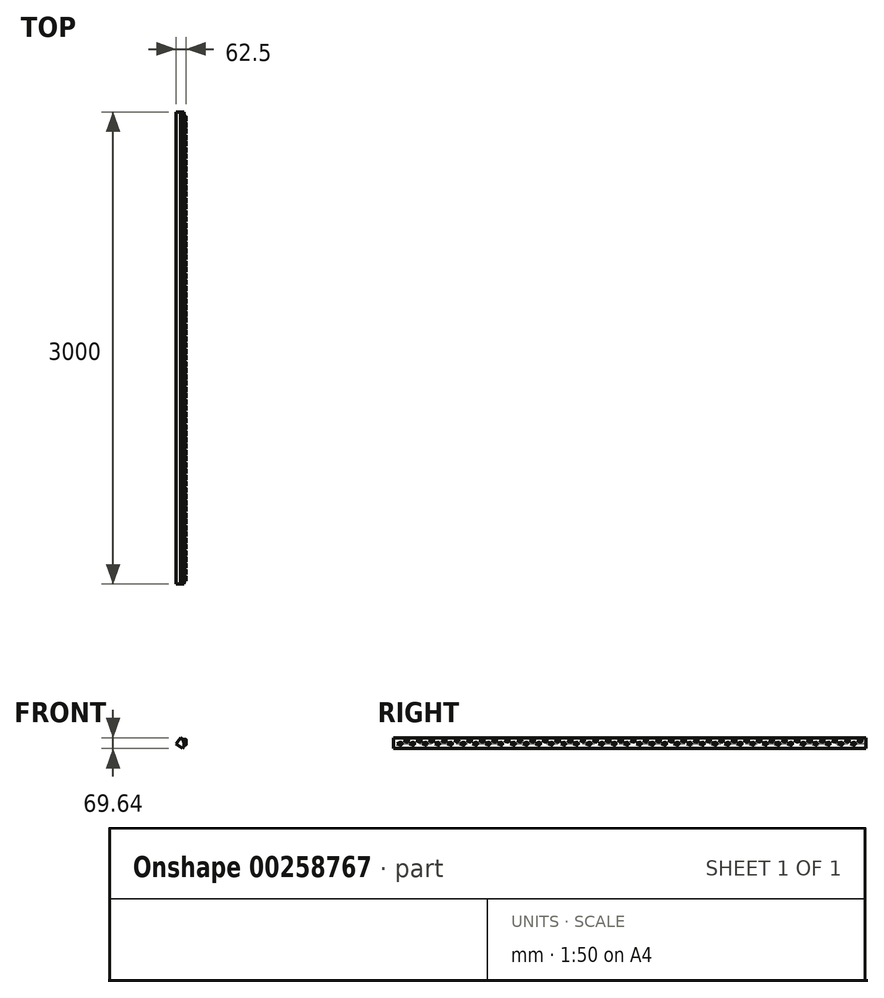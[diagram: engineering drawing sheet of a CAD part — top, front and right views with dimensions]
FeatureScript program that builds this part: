
annotation { "Feature Type Name" : "Feature", "Feature Type Description" : "" }
export const myFeature = defineFeature(function(context is Context, id is Id, definition is map)
    precondition{}
    {
        {
            var Q0;
            Q0=qCreatedBy(makeId("Front.planeOp"),FACE);
            var sketch = newSketch(context, id + "F0", { "sketchPlane" : qUnion([Q0])});
            skArc(sketch, "E0", {"start": v(40.96, -28.68) * mm, "mid": v(49.24, 8.68) * mm, "end": v(28.68, 40.96) * mm});
            skLineSegment(sketch, "E1", {"start": v(0, 0) * mm, "end": v(28.68, 40.96) * mm});
            skLineSegment(sketch, "E2", {"start": v(0, 0) * mm, "end": v(40.96, -28.68) * mm});
            skSolve(sketch);
        }
        {
            var Q0;
            Q0 = qSketchRegion(id + "F0", true);
            extrude(context, id + "F1", {"entities" : qUnion([Q0]), "oppositeDirection" : true, "depth" : 3000 * mm});
        }
        {
            var Q0;
            Q0=qCreatedBy(makeId("Right.planeOp"),FACE);
            cPlane(context, id + "F2", {"entities" : qUnion([Q0]), "cplaneType" : CPlaneType.OFFSET, "offset" : 50 * mm, "width" : 150 * mm, "height" : 150 * mm});
        }
        {
            var Q0;
            Q0=qCreatedBy(id+"F2.planeOp",FACE);
            var sketch = newSketch(context, id + "F3", { "sketchPlane" : qUnion([Q0])});
            skLineSegment(sketch, "E3", {"start": v(21.54, 0) * mm, "end": v(38.71, 10.26) * mm});
            skLineSegment(sketch, "E4", {"start": v(21.54, 0) * mm, "end": v(40.62, -6) * mm});
            skArc(sketch, "E5", {"start": v(40.62, -6) * mm, "mid": v(52.32, 3.61) * mm, "end": v(38.71, 10.26) * mm});
            skLineSegment(sketch, "E6.1.0.0", {"start": v(101.54, 0) * mm, "end": v(118.71, 10.26) * mm});
            skLineSegment(sketch, "E6.1.0.1", {"start": v(101.54, 0) * mm, "end": v(120.62, -6) * mm});
            skArc(sketch, "E6.1.0.2", {"start": v(120.62, -6) * mm, "mid": v(132.32, 3.61) * mm, "end": v(118.71, 10.26) * mm});
            skLineSegment(sketch, "E6.2.0.0", {"start": v(181.54, 0) * mm, "end": v(198.71, 10.26) * mm});
            skLineSegment(sketch, "E6.2.0.1", {"start": v(181.54, 0) * mm, "end": v(200.62, -6) * mm});
            skArc(sketch, "E6.2.0.2", {"start": v(200.62, -6) * mm, "mid": v(212.32, 3.61) * mm, "end": v(198.71, 10.26) * mm});
            skLineSegment(sketch, "E6.3.0.0", {"start": v(261.54, 0) * mm, "end": v(278.71, 10.26) * mm});
            skLineSegment(sketch, "E6.3.0.1", {"start": v(261.54, 0) * mm, "end": v(280.62, -6) * mm});
            skArc(sketch, "E6.3.0.2", {"start": v(280.62, -6) * mm, "mid": v(292.32, 3.61) * mm, "end": v(278.71, 10.26) * mm});
            skLineSegment(sketch, "E6.4.0.0", {"start": v(341.54, 0) * mm, "end": v(358.71, 10.26) * mm});
            skLineSegment(sketch, "E6.4.0.1", {"start": v(341.54, 0) * mm, "end": v(360.62, -6) * mm});
            skArc(sketch, "E6.4.0.2", {"start": v(360.62, -6) * mm, "mid": v(372.32, 3.61) * mm, "end": v(358.71, 10.26) * mm});
            skLineSegment(sketch, "E6.5.0.0", {"start": v(421.54, 0) * mm, "end": v(438.71, 10.26) * mm});
            skLineSegment(sketch, "E6.5.0.1", {"start": v(421.54, 0) * mm, "end": v(440.62, -6) * mm});
            skArc(sketch, "E6.5.0.2", {"start": v(440.62, -6) * mm, "mid": v(452.32, 3.61) * mm, "end": v(438.71, 10.26) * mm});
            skLineSegment(sketch, "E6.6.0.0", {"start": v(501.54, 0) * mm, "end": v(518.71, 10.26) * mm});
            skLineSegment(sketch, "E6.6.0.1", {"start": v(501.54, 0) * mm, "end": v(520.62, -6) * mm});
            skArc(sketch, "E6.6.0.2", {"start": v(520.62, -6) * mm, "mid": v(532.32, 3.61) * mm, "end": v(518.71, 10.26) * mm});
            skLineSegment(sketch, "E6.7.0.0", {"start": v(581.54, 0) * mm, "end": v(598.71, 10.26) * mm});
            skLineSegment(sketch, "E6.7.0.1", {"start": v(581.54, 0) * mm, "end": v(600.62, -6) * mm});
            skArc(sketch, "E6.7.0.2", {"start": v(600.62, -6) * mm, "mid": v(612.32, 3.61) * mm, "end": v(598.71, 10.26) * mm});
            skLineSegment(sketch, "E6.8.0.0", {"start": v(661.54, 0) * mm, "end": v(678.71, 10.26) * mm});
            skLineSegment(sketch, "E6.8.0.1", {"start": v(661.54, 0) * mm, "end": v(680.62, -6) * mm});
            skArc(sketch, "E6.8.0.2", {"start": v(680.62, -6) * mm, "mid": v(692.32, 3.61) * mm, "end": v(678.71, 10.26) * mm});
            skLineSegment(sketch, "E6.9.0.0", {"start": v(741.54, 0) * mm, "end": v(758.71, 10.26) * mm});
            skLineSegment(sketch, "E6.9.0.1", {"start": v(741.54, 0) * mm, "end": v(760.62, -6) * mm});
            skArc(sketch, "E6.9.0.2", {"start": v(760.62, -6) * mm, "mid": v(772.32, 3.61) * mm, "end": v(758.71, 10.26) * mm});
            skLineSegment(sketch, "E6.10.0.0", {"start": v(821.54, 0) * mm, "end": v(838.71, 10.26) * mm});
            skLineSegment(sketch, "E6.10.0.1", {"start": v(821.54, 0) * mm, "end": v(840.62, -6) * mm});
            skArc(sketch, "E6.10.0.2", {"start": v(840.62, -6) * mm, "mid": v(852.32, 3.61) * mm, "end": v(838.71, 10.26) * mm});
            skLineSegment(sketch, "E6.11.0.0", {"start": v(901.54, 0) * mm, "end": v(918.71, 10.26) * mm});
            skLineSegment(sketch, "E6.11.0.1", {"start": v(901.54, 0) * mm, "end": v(920.62, -6) * mm});
            skArc(sketch, "E6.11.0.2", {"start": v(920.62, -6) * mm, "mid": v(932.32, 3.61) * mm, "end": v(918.71, 10.26) * mm});
            skLineSegment(sketch, "E6.12.0.0", {"start": v(981.54, 0) * mm, "end": v(998.71, 10.26) * mm});
            skLineSegment(sketch, "E6.12.0.1", {"start": v(981.54, 0) * mm, "end": v(1000.62, -6) * mm});
            skArc(sketch, "E6.12.0.2", {"start": v(1000.62, -6) * mm, "mid": v(1012.32, 3.61) * mm, "end": v(998.71, 10.26) * mm});
            skLineSegment(sketch, "E6.13.0.0", {"start": v(1061.54, 0) * mm, "end": v(1078.71, 10.26) * mm});
            skLineSegment(sketch, "E6.13.0.1", {"start": v(1061.54, 0) * mm, "end": v(1080.62, -6) * mm});
            skArc(sketch, "E6.13.0.2", {"start": v(1080.62, -6) * mm, "mid": v(1092.32, 3.61) * mm, "end": v(1078.71, 10.26) * mm});
            skLineSegment(sketch, "E6.14.0.0", {"start": v(1141.54, 0) * mm, "end": v(1158.71, 10.26) * mm});
            skLineSegment(sketch, "E6.14.0.1", {"start": v(1141.54, 0) * mm, "end": v(1160.62, -6) * mm});
            skArc(sketch, "E6.14.0.2", {"start": v(1160.62, -6) * mm, "mid": v(1172.32, 3.61) * mm, "end": v(1158.71, 10.26) * mm});
            skLineSegment(sketch, "E6.15.0.0", {"start": v(1221.54, 0) * mm, "end": v(1238.71, 10.26) * mm});
            skLineSegment(sketch, "E6.15.0.1", {"start": v(1221.54, 0) * mm, "end": v(1240.62, -6) * mm});
            skArc(sketch, "E6.15.0.2", {"start": v(1240.62, -6) * mm, "mid": v(1252.32, 3.61) * mm, "end": v(1238.71, 10.26) * mm});
            skLineSegment(sketch, "E6.16.0.0", {"start": v(1301.54, 0) * mm, "end": v(1318.71, 10.26) * mm});
            skLineSegment(sketch, "E6.16.0.1", {"start": v(1301.54, 0) * mm, "end": v(1320.62, -6) * mm});
            skArc(sketch, "E6.16.0.2", {"start": v(1320.62, -6) * mm, "mid": v(1332.32, 3.61) * mm, "end": v(1318.71, 10.26) * mm});
            skLineSegment(sketch, "E6.17.0.0", {"start": v(1381.54, 0) * mm, "end": v(1398.71, 10.26) * mm});
            skLineSegment(sketch, "E6.17.0.1", {"start": v(1381.54, 0) * mm, "end": v(1400.62, -6) * mm});
            skArc(sketch, "E6.17.0.2", {"start": v(1400.62, -6) * mm, "mid": v(1412.32, 3.61) * mm, "end": v(1398.71, 10.26) * mm});
            skLineSegment(sketch, "E6.18.0.0", {"start": v(1461.54, 0) * mm, "end": v(1478.71, 10.26) * mm});
            skLineSegment(sketch, "E6.18.0.1", {"start": v(1461.54, 0) * mm, "end": v(1480.62, -6) * mm});
            skArc(sketch, "E6.18.0.2", {"start": v(1480.62, -6) * mm, "mid": v(1492.32, 3.61) * mm, "end": v(1478.71, 10.26) * mm});
            skLineSegment(sketch, "E6.19.0.0", {"start": v(1541.54, 0) * mm, "end": v(1558.71, 10.26) * mm});
            skLineSegment(sketch, "E6.19.0.1", {"start": v(1541.54, 0) * mm, "end": v(1560.62, -6) * mm});
            skArc(sketch, "E6.19.0.2", {"start": v(1560.62, -6) * mm, "mid": v(1572.32, 3.61) * mm, "end": v(1558.71, 10.26) * mm});
            skLineSegment(sketch, "E6.20.0.0", {"start": v(1621.54, 0) * mm, "end": v(1638.71, 10.26) * mm});
            skLineSegment(sketch, "E6.20.0.1", {"start": v(1621.54, 0) * mm, "end": v(1640.62, -6) * mm});
            skArc(sketch, "E6.20.0.2", {"start": v(1640.62, -6) * mm, "mid": v(1652.32, 3.61) * mm, "end": v(1638.71, 10.26) * mm});
            skLineSegment(sketch, "E6.21.0.0", {"start": v(1701.54, 0) * mm, "end": v(1718.71, 10.26) * mm});
            skLineSegment(sketch, "E6.21.0.1", {"start": v(1701.54, 0) * mm, "end": v(1720.62, -6) * mm});
            skArc(sketch, "E6.21.0.2", {"start": v(1720.62, -6) * mm, "mid": v(1732.32, 3.61) * mm, "end": v(1718.71, 10.26) * mm});
            skLineSegment(sketch, "E6.22.0.0", {"start": v(1781.54, 0) * mm, "end": v(1798.71, 10.26) * mm});
            skLineSegment(sketch, "E6.22.0.1", {"start": v(1781.54, 0) * mm, "end": v(1800.62, -6) * mm});
            skArc(sketch, "E6.22.0.2", {"start": v(1800.62, -6) * mm, "mid": v(1812.32, 3.61) * mm, "end": v(1798.71, 10.26) * mm});
            skLineSegment(sketch, "E6.23.0.0", {"start": v(1861.54, 0) * mm, "end": v(1878.71, 10.26) * mm});
            skLineSegment(sketch, "E6.23.0.1", {"start": v(1861.54, 0) * mm, "end": v(1880.62, -6) * mm});
            skArc(sketch, "E6.23.0.2", {"start": v(1880.62, -6) * mm, "mid": v(1892.32, 3.61) * mm, "end": v(1878.71, 10.26) * mm});
            skLineSegment(sketch, "E6.24.0.0", {"start": v(1941.54, 0) * mm, "end": v(1958.71, 10.26) * mm});
            skLineSegment(sketch, "E6.24.0.1", {"start": v(1941.54, 0) * mm, "end": v(1960.62, -6) * mm});
            skArc(sketch, "E6.24.0.2", {"start": v(1960.62, -6) * mm, "mid": v(1972.32, 3.61) * mm, "end": v(1958.71, 10.26) * mm});
            skLineSegment(sketch, "E6.25.0.0", {"start": v(2021.54, 0) * mm, "end": v(2038.71, 10.26) * mm});
            skLineSegment(sketch, "E6.25.0.1", {"start": v(2021.54, 0) * mm, "end": v(2040.62, -6) * mm});
            skArc(sketch, "E6.25.0.2", {"start": v(2040.62, -6) * mm, "mid": v(2052.32, 3.61) * mm, "end": v(2038.71, 10.26) * mm});
            skLineSegment(sketch, "E6.26.0.0", {"start": v(2101.54, 0) * mm, "end": v(2118.71, 10.26) * mm});
            skLineSegment(sketch, "E6.26.0.1", {"start": v(2101.54, 0) * mm, "end": v(2120.62, -6) * mm});
            skArc(sketch, "E6.26.0.2", {"start": v(2120.62, -6) * mm, "mid": v(2132.32, 3.61) * mm, "end": v(2118.71, 10.26) * mm});
            skLineSegment(sketch, "E6.27.0.0", {"start": v(2181.54, 0) * mm, "end": v(2198.71, 10.26) * mm});
            skLineSegment(sketch, "E6.27.0.1", {"start": v(2181.54, 0) * mm, "end": v(2200.62, -6) * mm});
            skArc(sketch, "E6.27.0.2", {"start": v(2200.62, -6) * mm, "mid": v(2212.32, 3.61) * mm, "end": v(2198.71, 10.26) * mm});
            skLineSegment(sketch, "E6.28.0.0", {"start": v(2261.54, 0) * mm, "end": v(2278.71, 10.26) * mm});
            skLineSegment(sketch, "E6.28.0.1", {"start": v(2261.54, 0) * mm, "end": v(2280.62, -6) * mm});
            skArc(sketch, "E6.28.0.2", {"start": v(2280.62, -6) * mm, "mid": v(2292.32, 3.61) * mm, "end": v(2278.71, 10.26) * mm});
            skLineSegment(sketch, "E6.29.0.0", {"start": v(2341.54, 0) * mm, "end": v(2358.71, 10.26) * mm});
            skLineSegment(sketch, "E6.29.0.1", {"start": v(2341.54, 0) * mm, "end": v(2360.62, -6) * mm});
            skArc(sketch, "E6.29.0.2", {"start": v(2360.62, -6) * mm, "mid": v(2372.32, 3.61) * mm, "end": v(2358.71, 10.26) * mm});
            skLineSegment(sketch, "E6.direction1", {"start": v(21.54, 0) * mm, "end": v(101.54, 0) * mm, "construction": true});
            skLineSegment(sketch, "E7.0.30.0", {"start": v(2421.54, 0) * mm, "end": v(2438.71, 10.26) * mm});
            skLineSegment(sketch, "E7.3.30.0", {"start": v(2421.54, 0) * mm, "end": v(2440.62, -6) * mm});
            skArc(sketch, "E7.6.30.0", {"start": v(2440.62, -6) * mm, "mid": v(2452.32, 3.61) * mm, "end": v(2438.71, 10.26) * mm});
            skLineSegment(sketch, "E7.0.31.0", {"start": v(2501.54, 0) * mm, "end": v(2518.71, 10.26) * mm});
            skLineSegment(sketch, "E7.3.31.0", {"start": v(2501.54, 0) * mm, "end": v(2520.62, -6) * mm});
            skArc(sketch, "E7.6.31.0", {"start": v(2520.62, -6) * mm, "mid": v(2532.32, 3.61) * mm, "end": v(2518.71, 10.26) * mm});
            skLineSegment(sketch, "E7.0.32.0", {"start": v(2581.54, 0) * mm, "end": v(2598.71, 10.26) * mm});
            skLineSegment(sketch, "E7.3.32.0", {"start": v(2581.54, 0) * mm, "end": v(2600.62, -6) * mm});
            skArc(sketch, "E7.6.32.0", {"start": v(2600.62, -6) * mm, "mid": v(2612.32, 3.61) * mm, "end": v(2598.71, 10.26) * mm});
            skLineSegment(sketch, "E7.0.33.0", {"start": v(2661.54, 0) * mm, "end": v(2678.71, 10.26) * mm});
            skLineSegment(sketch, "E7.3.33.0", {"start": v(2661.54, 0) * mm, "end": v(2680.62, -6) * mm});
            skArc(sketch, "E7.6.33.0", {"start": v(2680.62, -6) * mm, "mid": v(2692.32, 3.61) * mm, "end": v(2678.71, 10.26) * mm});
            skLineSegment(sketch, "E7.0.34.0", {"start": v(2741.54, 0) * mm, "end": v(2758.71, 10.26) * mm});
            skLineSegment(sketch, "E7.3.34.0", {"start": v(2741.54, 0) * mm, "end": v(2760.62, -6) * mm});
            skArc(sketch, "E7.6.34.0", {"start": v(2760.62, -6) * mm, "mid": v(2772.32, 3.61) * mm, "end": v(2758.71, 10.26) * mm});
            skLineSegment(sketch, "E8.0.35.0", {"start": v(2821.54, 0) * mm, "end": v(2838.71, 10.26) * mm});
            skLineSegment(sketch, "E8.3.35.0", {"start": v(2821.54, 0) * mm, "end": v(2840.62, -6) * mm});
            skArc(sketch, "E8.6.35.0", {"start": v(2840.62, -6) * mm, "mid": v(2852.32, 3.61) * mm, "end": v(2838.71, 10.26) * mm});
            skLineSegment(sketch, "E8.0.36.0", {"start": v(2901.54, 0) * mm, "end": v(2918.71, 10.26) * mm});
            skLineSegment(sketch, "E8.3.36.0", {"start": v(2901.54, 0) * mm, "end": v(2920.62, -6) * mm});
            skArc(sketch, "E8.6.36.0", {"start": v(2920.62, -6) * mm, "mid": v(2932.32, 3.61) * mm, "end": v(2918.71, 10.26) * mm});
            skLineSegment(sketch, "E9", {"start": v(62.38, 22.39) * mm, "end": v(80.62, 30.6) * mm});
            skLineSegment(sketch, "E10", {"start": v(62.38, 22.39) * mm, "end": v(80.62, 14.18) * mm});
            skArc(sketch, "E11", {"start": v(80.62, 14.18) * mm, "mid": v(93.31, 22.39) * mm, "end": v(80.62, 30.6) * mm});
            skLineSegment(sketch, "E12.1.0.0", {"start": v(142.38, 22.39) * mm, "end": v(160.62, 30.6) * mm});
            skLineSegment(sketch, "E12.1.0.1", {"start": v(142.38, 22.39) * mm, "end": v(160.62, 14.18) * mm});
            skArc(sketch, "E12.1.0.2", {"start": v(160.62, 14.18) * mm, "mid": v(173.31, 22.39) * mm, "end": v(160.62, 30.6) * mm});
            skLineSegment(sketch, "E12.2.0.0", {"start": v(222.38, 22.39) * mm, "end": v(240.62, 30.6) * mm});
            skLineSegment(sketch, "E12.2.0.1", {"start": v(222.38, 22.39) * mm, "end": v(240.62, 14.18) * mm});
            skArc(sketch, "E12.2.0.2", {"start": v(240.62, 14.18) * mm, "mid": v(253.31, 22.39) * mm, "end": v(240.62, 30.6) * mm});
            skLineSegment(sketch, "E12.3.0.0", {"start": v(302.38, 22.39) * mm, "end": v(320.62, 30.6) * mm});
            skLineSegment(sketch, "E12.3.0.1", {"start": v(302.38, 22.39) * mm, "end": v(320.62, 14.18) * mm});
            skArc(sketch, "E12.3.0.2", {"start": v(320.62, 14.18) * mm, "mid": v(333.31, 22.39) * mm, "end": v(320.62, 30.6) * mm});
            skLineSegment(sketch, "E12.4.0.0", {"start": v(382.38, 22.39) * mm, "end": v(400.62, 30.6) * mm});
            skLineSegment(sketch, "E12.4.0.1", {"start": v(382.38, 22.39) * mm, "end": v(400.62, 14.18) * mm});
            skArc(sketch, "E12.4.0.2", {"start": v(400.62, 14.18) * mm, "mid": v(413.31, 22.39) * mm, "end": v(400.62, 30.6) * mm});
            skLineSegment(sketch, "E12.5.0.0", {"start": v(462.38, 22.39) * mm, "end": v(480.62, 30.6) * mm});
            skLineSegment(sketch, "E12.5.0.1", {"start": v(462.38, 22.39) * mm, "end": v(480.62, 14.18) * mm});
            skArc(sketch, "E12.5.0.2", {"start": v(480.62, 14.18) * mm, "mid": v(493.31, 22.39) * mm, "end": v(480.62, 30.6) * mm});
            skLineSegment(sketch, "E12.6.0.0", {"start": v(542.38, 22.39) * mm, "end": v(560.62, 30.6) * mm});
            skLineSegment(sketch, "E12.6.0.1", {"start": v(542.38, 22.39) * mm, "end": v(560.62, 14.18) * mm});
            skArc(sketch, "E12.6.0.2", {"start": v(560.62, 14.18) * mm, "mid": v(573.31, 22.39) * mm, "end": v(560.62, 30.6) * mm});
            skLineSegment(sketch, "E12.7.0.0", {"start": v(622.38, 22.39) * mm, "end": v(640.62, 30.6) * mm});
            skLineSegment(sketch, "E12.7.0.1", {"start": v(622.38, 22.39) * mm, "end": v(640.62, 14.18) * mm});
            skArc(sketch, "E12.7.0.2", {"start": v(640.62, 14.18) * mm, "mid": v(653.31, 22.39) * mm, "end": v(640.62, 30.6) * mm});
            skLineSegment(sketch, "E12.8.0.0", {"start": v(702.38, 22.39) * mm, "end": v(720.62, 30.6) * mm});
            skLineSegment(sketch, "E12.8.0.1", {"start": v(702.38, 22.39) * mm, "end": v(720.62, 14.18) * mm});
            skArc(sketch, "E12.8.0.2", {"start": v(720.62, 14.18) * mm, "mid": v(733.31, 22.39) * mm, "end": v(720.62, 30.6) * mm});
            skLineSegment(sketch, "E12.9.0.0", {"start": v(782.38, 22.39) * mm, "end": v(800.62, 30.6) * mm});
            skLineSegment(sketch, "E12.9.0.1", {"start": v(782.38, 22.39) * mm, "end": v(800.62, 14.18) * mm});
            skArc(sketch, "E12.9.0.2", {"start": v(800.62, 14.18) * mm, "mid": v(813.31, 22.39) * mm, "end": v(800.62, 30.6) * mm});
            skLineSegment(sketch, "E12.10.0.0", {"start": v(862.38, 22.39) * mm, "end": v(880.62, 30.6) * mm});
            skLineSegment(sketch, "E12.10.0.1", {"start": v(862.38, 22.39) * mm, "end": v(880.62, 14.18) * mm});
            skArc(sketch, "E12.10.0.2", {"start": v(880.62, 14.18) * mm, "mid": v(893.31, 22.39) * mm, "end": v(880.62, 30.6) * mm});
            skLineSegment(sketch, "E12.11.0.0", {"start": v(942.38, 22.39) * mm, "end": v(960.62, 30.6) * mm});
            skLineSegment(sketch, "E12.11.0.1", {"start": v(942.38, 22.39) * mm, "end": v(960.62, 14.18) * mm});
            skArc(sketch, "E12.11.0.2", {"start": v(960.62, 14.18) * mm, "mid": v(973.31, 22.39) * mm, "end": v(960.62, 30.6) * mm});
            skLineSegment(sketch, "E12.12.0.0", {"start": v(1022.38, 22.39) * mm, "end": v(1040.62, 30.6) * mm});
            skLineSegment(sketch, "E12.12.0.1", {"start": v(1022.38, 22.39) * mm, "end": v(1040.62, 14.18) * mm});
            skArc(sketch, "E12.12.0.2", {"start": v(1040.62, 14.18) * mm, "mid": v(1053.31, 22.39) * mm, "end": v(1040.62, 30.6) * mm});
            skLineSegment(sketch, "E12.13.0.0", {"start": v(1102.38, 22.39) * mm, "end": v(1120.62, 30.6) * mm});
            skLineSegment(sketch, "E12.13.0.1", {"start": v(1102.38, 22.39) * mm, "end": v(1120.62, 14.18) * mm});
            skArc(sketch, "E12.13.0.2", {"start": v(1120.62, 14.18) * mm, "mid": v(1133.31, 22.39) * mm, "end": v(1120.62, 30.6) * mm});
            skLineSegment(sketch, "E12.14.0.0", {"start": v(1182.38, 22.39) * mm, "end": v(1200.62, 30.6) * mm});
            skLineSegment(sketch, "E12.14.0.1", {"start": v(1182.38, 22.39) * mm, "end": v(1200.62, 14.18) * mm});
            skArc(sketch, "E12.14.0.2", {"start": v(1200.62, 14.18) * mm, "mid": v(1213.31, 22.39) * mm, "end": v(1200.62, 30.6) * mm});
            skLineSegment(sketch, "E12.15.0.0", {"start": v(1262.38, 22.39) * mm, "end": v(1280.62, 30.6) * mm});
            skLineSegment(sketch, "E12.15.0.1", {"start": v(1262.38, 22.39) * mm, "end": v(1280.62, 14.18) * mm});
            skArc(sketch, "E12.15.0.2", {"start": v(1280.62, 14.18) * mm, "mid": v(1293.31, 22.39) * mm, "end": v(1280.62, 30.6) * mm});
            skLineSegment(sketch, "E12.16.0.0", {"start": v(1342.38, 22.39) * mm, "end": v(1360.62, 30.6) * mm});
            skLineSegment(sketch, "E12.16.0.1", {"start": v(1342.38, 22.39) * mm, "end": v(1360.62, 14.18) * mm});
            skArc(sketch, "E12.16.0.2", {"start": v(1360.62, 14.18) * mm, "mid": v(1373.31, 22.39) * mm, "end": v(1360.62, 30.6) * mm});
            skLineSegment(sketch, "E12.17.0.0", {"start": v(1422.38, 22.39) * mm, "end": v(1440.62, 30.6) * mm});
            skLineSegment(sketch, "E12.17.0.1", {"start": v(1422.38, 22.39) * mm, "end": v(1440.62, 14.18) * mm});
            skArc(sketch, "E12.17.0.2", {"start": v(1440.62, 14.18) * mm, "mid": v(1453.31, 22.39) * mm, "end": v(1440.62, 30.6) * mm});
            skLineSegment(sketch, "E12.18.0.0", {"start": v(1502.38, 22.39) * mm, "end": v(1520.62, 30.6) * mm});
            skLineSegment(sketch, "E12.18.0.1", {"start": v(1502.38, 22.39) * mm, "end": v(1520.62, 14.18) * mm});
            skArc(sketch, "E12.18.0.2", {"start": v(1520.62, 14.18) * mm, "mid": v(1533.31, 22.39) * mm, "end": v(1520.62, 30.6) * mm});
            skLineSegment(sketch, "E12.19.0.0", {"start": v(1582.38, 22.39) * mm, "end": v(1600.62, 30.6) * mm});
            skLineSegment(sketch, "E12.19.0.1", {"start": v(1582.38, 22.39) * mm, "end": v(1600.62, 14.18) * mm});
            skArc(sketch, "E12.19.0.2", {"start": v(1600.62, 14.18) * mm, "mid": v(1613.31, 22.39) * mm, "end": v(1600.62, 30.6) * mm});
            skLineSegment(sketch, "E12.20.0.0", {"start": v(1662.38, 22.39) * mm, "end": v(1680.62, 30.6) * mm});
            skLineSegment(sketch, "E12.20.0.1", {"start": v(1662.38, 22.39) * mm, "end": v(1680.62, 14.18) * mm});
            skArc(sketch, "E12.20.0.2", {"start": v(1680.62, 14.18) * mm, "mid": v(1693.31, 22.39) * mm, "end": v(1680.62, 30.6) * mm});
            skLineSegment(sketch, "E12.21.0.0", {"start": v(1742.38, 22.39) * mm, "end": v(1760.62, 30.6) * mm});
            skLineSegment(sketch, "E12.21.0.1", {"start": v(1742.38, 22.39) * mm, "end": v(1760.62, 14.18) * mm});
            skArc(sketch, "E12.21.0.2", {"start": v(1760.62, 14.18) * mm, "mid": v(1773.31, 22.39) * mm, "end": v(1760.62, 30.6) * mm});
            skLineSegment(sketch, "E12.22.0.0", {"start": v(1822.38, 22.39) * mm, "end": v(1840.62, 30.6) * mm});
            skLineSegment(sketch, "E12.22.0.1", {"start": v(1822.38, 22.39) * mm, "end": v(1840.62, 14.18) * mm});
            skArc(sketch, "E12.22.0.2", {"start": v(1840.62, 14.18) * mm, "mid": v(1853.31, 22.39) * mm, "end": v(1840.62, 30.6) * mm});
            skLineSegment(sketch, "E12.23.0.0", {"start": v(1902.38, 22.39) * mm, "end": v(1920.62, 30.6) * mm});
            skLineSegment(sketch, "E12.23.0.1", {"start": v(1902.38, 22.39) * mm, "end": v(1920.62, 14.18) * mm});
            skArc(sketch, "E12.23.0.2", {"start": v(1920.62, 14.18) * mm, "mid": v(1933.31, 22.39) * mm, "end": v(1920.62, 30.6) * mm});
            skLineSegment(sketch, "E12.24.0.0", {"start": v(1982.38, 22.39) * mm, "end": v(2000.62, 30.6) * mm});
            skLineSegment(sketch, "E12.24.0.1", {"start": v(1982.38, 22.39) * mm, "end": v(2000.62, 14.18) * mm});
            skArc(sketch, "E12.24.0.2", {"start": v(2000.62, 14.18) * mm, "mid": v(2013.31, 22.39) * mm, "end": v(2000.62, 30.6) * mm});
            skLineSegment(sketch, "E12.25.0.0", {"start": v(2062.38, 22.39) * mm, "end": v(2080.62, 30.6) * mm});
            skLineSegment(sketch, "E12.25.0.1", {"start": v(2062.38, 22.39) * mm, "end": v(2080.62, 14.18) * mm});
            skArc(sketch, "E12.25.0.2", {"start": v(2080.62, 14.18) * mm, "mid": v(2093.31, 22.39) * mm, "end": v(2080.62, 30.6) * mm});
            skLineSegment(sketch, "E12.26.0.0", {"start": v(2142.38, 22.39) * mm, "end": v(2160.62, 30.6) * mm});
            skLineSegment(sketch, "E12.26.0.1", {"start": v(2142.38, 22.39) * mm, "end": v(2160.62, 14.18) * mm});
            skArc(sketch, "E12.26.0.2", {"start": v(2160.62, 14.18) * mm, "mid": v(2173.31, 22.39) * mm, "end": v(2160.62, 30.6) * mm});
            skLineSegment(sketch, "E12.27.0.0", {"start": v(2222.38, 22.39) * mm, "end": v(2240.62, 30.6) * mm});
            skLineSegment(sketch, "E12.27.0.1", {"start": v(2222.38, 22.39) * mm, "end": v(2240.62, 14.18) * mm});
            skArc(sketch, "E12.27.0.2", {"start": v(2240.62, 14.18) * mm, "mid": v(2253.31, 22.39) * mm, "end": v(2240.62, 30.6) * mm});
            skLineSegment(sketch, "E12.28.0.0", {"start": v(2302.38, 22.39) * mm, "end": v(2320.62, 30.6) * mm});
            skLineSegment(sketch, "E12.28.0.1", {"start": v(2302.38, 22.39) * mm, "end": v(2320.62, 14.18) * mm});
            skArc(sketch, "E12.28.0.2", {"start": v(2320.62, 14.18) * mm, "mid": v(2333.31, 22.39) * mm, "end": v(2320.62, 30.6) * mm});
            skLineSegment(sketch, "E12.29.0.0", {"start": v(2382.38, 22.39) * mm, "end": v(2400.62, 30.6) * mm});
            skLineSegment(sketch, "E12.29.0.1", {"start": v(2382.38, 22.39) * mm, "end": v(2400.62, 14.18) * mm});
            skArc(sketch, "E12.29.0.2", {"start": v(2400.62, 14.18) * mm, "mid": v(2413.31, 22.39) * mm, "end": v(2400.62, 30.6) * mm});
            skLineSegment(sketch, "E12.30.0.0", {"start": v(2462.38, 22.39) * mm, "end": v(2480.62, 30.6) * mm});
            skLineSegment(sketch, "E12.30.0.1", {"start": v(2462.38, 22.39) * mm, "end": v(2480.62, 14.18) * mm});
            skArc(sketch, "E12.30.0.2", {"start": v(2480.62, 14.18) * mm, "mid": v(2493.31, 22.39) * mm, "end": v(2480.62, 30.6) * mm});
            skLineSegment(sketch, "E12.31.0.0", {"start": v(2542.38, 22.39) * mm, "end": v(2560.62, 30.6) * mm});
            skLineSegment(sketch, "E12.31.0.1", {"start": v(2542.38, 22.39) * mm, "end": v(2560.62, 14.18) * mm});
            skArc(sketch, "E12.31.0.2", {"start": v(2560.62, 14.18) * mm, "mid": v(2573.31, 22.39) * mm, "end": v(2560.62, 30.6) * mm});
            skLineSegment(sketch, "E12.32.0.0", {"start": v(2622.38, 22.39) * mm, "end": v(2640.62, 30.6) * mm});
            skLineSegment(sketch, "E12.32.0.1", {"start": v(2622.38, 22.39) * mm, "end": v(2640.62, 14.18) * mm});
            skArc(sketch, "E12.32.0.2", {"start": v(2640.62, 14.18) * mm, "mid": v(2653.31, 22.39) * mm, "end": v(2640.62, 30.6) * mm});
            skLineSegment(sketch, "E12.33.0.0", {"start": v(2702.38, 22.39) * mm, "end": v(2720.62, 30.6) * mm});
            skLineSegment(sketch, "E12.33.0.1", {"start": v(2702.38, 22.39) * mm, "end": v(2720.62, 14.18) * mm});
            skArc(sketch, "E12.33.0.2", {"start": v(2720.62, 14.18) * mm, "mid": v(2733.31, 22.39) * mm, "end": v(2720.62, 30.6) * mm});
            skLineSegment(sketch, "E12.34.0.0", {"start": v(2782.38, 22.39) * mm, "end": v(2800.62, 30.6) * mm});
            skLineSegment(sketch, "E12.34.0.1", {"start": v(2782.38, 22.39) * mm, "end": v(2800.62, 14.18) * mm});
            skArc(sketch, "E12.34.0.2", {"start": v(2800.62, 14.18) * mm, "mid": v(2813.31, 22.39) * mm, "end": v(2800.62, 30.6) * mm});
            skLineSegment(sketch, "E12.35.0.0", {"start": v(2862.38, 22.39) * mm, "end": v(2880.62, 30.6) * mm});
            skLineSegment(sketch, "E12.35.0.1", {"start": v(2862.38, 22.39) * mm, "end": v(2880.62, 14.18) * mm});
            skArc(sketch, "E12.35.0.2", {"start": v(2880.62, 14.18) * mm, "mid": v(2893.31, 22.39) * mm, "end": v(2880.62, 30.6) * mm});
            skLineSegment(sketch, "E12.36.0.0", {"start": v(2942.38, 22.39) * mm, "end": v(2960.62, 30.6) * mm});
            skLineSegment(sketch, "E12.36.0.1", {"start": v(2942.38, 22.39) * mm, "end": v(2960.62, 14.18) * mm});
            skArc(sketch, "E12.36.0.2", {"start": v(2960.62, 14.18) * mm, "mid": v(2973.31, 22.39) * mm, "end": v(2960.62, 30.6) * mm});
            skLineSegment(sketch, "E12.direction1", {"start": v(62.38, 22.39) * mm, "end": v(142.38, 22.39) * mm, "construction": true});
            skSolve(sketch);
        }
        {
            var Q0;
            Q0=makeQuery(id+"F3.imprint","IMPRINT",FACE,{"disambiguationData":[TD([[makeQuery(id+"F3.imprint","IMPRINT",EDGE,{"derivedFrom":sQuery(id+"F3.wireOp",EDGE,"VTlFpyJf-uL4w-auID-Xrw3-4fCM1R4orrIX")}),-1.0]])]});
            var Q1;
            Q1=makeQuery(id+"F3.imprint","IMPRINT",FACE,{"disambiguationData":[TD([[makeQuery(id+"F3.imprint","IMPRINT",EDGE,{"derivedFrom":sQuery(id+"F3.wireOp",EDGE,"E3")}),-1.0]])]});
            var Q2;
            Q2=makeQuery(id+"F3.imprint","IMPRINT",FACE,{"disambiguationData":[TD([[makeQuery(id+"F3.imprint","IMPRINT",EDGE,{"derivedFrom":sQuery(id+"F3.wireOp",EDGE,"E6.2.0.0")}),-1.0]])]});
            var Q3;
            Q3=makeQuery(id+"F3.imprint","IMPRINT",FACE,{"disambiguationData":[TD([[makeQuery(id+"F3.imprint","IMPRINT",EDGE,{"derivedFrom":sQuery(id+"F3.wireOp",EDGE,"E6.3.0.0")}),-1.0]])]});
            var Q4;
            Q4=makeQuery(id+"F3.imprint","IMPRINT",FACE,{"disambiguationData":[TD([[makeQuery(id+"F3.imprint","IMPRINT",EDGE,{"derivedFrom":sQuery(id+"F3.wireOp",EDGE,"E6.4.0.0")}),-1.0]])]});
            var Q5;
            Q5=makeQuery(id+"F3.imprint","IMPRINT",FACE,{"disambiguationData":[TD([[makeQuery(id+"F3.imprint","IMPRINT",EDGE,{"derivedFrom":sQuery(id+"F3.wireOp",EDGE,"E6.5.0.0")}),-1.0]])]});
            var Q6;
            Q6=makeQuery(id+"F3.imprint","IMPRINT",FACE,{"disambiguationData":[TD([[makeQuery(id+"F3.imprint","IMPRINT",EDGE,{"derivedFrom":sQuery(id+"F3.wireOp",EDGE,"E6.6.0.0")}),-1.0]])]});
            var Q7;
            Q7=makeQuery(id+"F3.imprint","IMPRINT",FACE,{"disambiguationData":[TD([[makeQuery(id+"F3.imprint","IMPRINT",EDGE,{"derivedFrom":sQuery(id+"F3.wireOp",EDGE,"E6.7.0.0")}),-1.0]])]});
            var Q8;
            Q8=makeQuery(id+"F3.imprint","IMPRINT",FACE,{"disambiguationData":[TD([[makeQuery(id+"F3.imprint","IMPRINT",EDGE,{"derivedFrom":sQuery(id+"F3.wireOp",EDGE,"E6.8.0.0")}),-1.0]])]});
            var Q9;
            Q9=makeQuery(id+"F3.imprint","IMPRINT",FACE,{"disambiguationData":[TD([[makeQuery(id+"F3.imprint","IMPRINT",EDGE,{"derivedFrom":sQuery(id+"F3.wireOp",EDGE,"E6.9.0.0")}),-1.0]])]});
            var Q10;
            Q10=makeQuery(id+"F3.imprint","IMPRINT",FACE,{"disambiguationData":[TD([[makeQuery(id+"F3.imprint","IMPRINT",EDGE,{"derivedFrom":sQuery(id+"F3.wireOp",EDGE,"E6.10.0.0")}),-1.0]])]});
            var Q11;
            Q11=makeQuery(id+"F3.imprint","IMPRINT",FACE,{"disambiguationData":[TD([[makeQuery(id+"F3.imprint","IMPRINT",EDGE,{"derivedFrom":sQuery(id+"F3.wireOp",EDGE,"E6.1.0.0")}),-1.0]])]});
            var Q12;
            Q12=makeQuery(id+"F3.imprint","IMPRINT",FACE,{"disambiguationData":[TD([[makeQuery(id+"F3.imprint","IMPRINT",EDGE,{"derivedFrom":sQuery(id+"F3.wireOp",EDGE,"E6.11.0.0")}),-1.0]])]});
            var Q13;
            Q13=makeQuery(id+"F3.imprint","IMPRINT",FACE,{"disambiguationData":[TD([[makeQuery(id+"F3.imprint","IMPRINT",EDGE,{"derivedFrom":sQuery(id+"F3.wireOp",EDGE,"E6.12.0.0")}),-1.0]])]});
            var Q14;
            Q14=makeQuery(id+"F3.imprint","IMPRINT",FACE,{"disambiguationData":[TD([[makeQuery(id+"F3.imprint","IMPRINT",EDGE,{"derivedFrom":sQuery(id+"F3.wireOp",EDGE,"E6.13.0.0")}),-1.0]])]});
            var Q15;
            Q15=makeQuery(id+"F3.imprint","IMPRINT",FACE,{"disambiguationData":[TD([[makeQuery(id+"F3.imprint","IMPRINT",EDGE,{"derivedFrom":sQuery(id+"F3.wireOp",EDGE,"E6.14.0.0")}),-1.0]])]});
            var Q16;
            Q16=makeQuery(id+"F3.imprint","IMPRINT",FACE,{"disambiguationData":[TD([[makeQuery(id+"F3.imprint","IMPRINT",EDGE,{"derivedFrom":sQuery(id+"F3.wireOp",EDGE,"E6.16.0.0")}),-1.0]])]});
            var Q17;
            Q17=makeQuery(id+"F3.imprint","IMPRINT",FACE,{"disambiguationData":[TD([[makeQuery(id+"F3.imprint","IMPRINT",EDGE,{"derivedFrom":sQuery(id+"F3.wireOp",EDGE,"E6.17.0.0")}),-1.0]])]});
            var Q18;
            Q18=makeQuery(id+"F3.imprint","IMPRINT",FACE,{"disambiguationData":[TD([[makeQuery(id+"F3.imprint","IMPRINT",EDGE,{"derivedFrom":sQuery(id+"F3.wireOp",EDGE,"E6.18.0.0")}),-1.0]])]});
            var Q19;
            Q19=makeQuery(id+"F3.imprint","IMPRINT",FACE,{"disambiguationData":[TD([[makeQuery(id+"F3.imprint","IMPRINT",EDGE,{"derivedFrom":sQuery(id+"F3.wireOp",EDGE,"E6.19.0.0")}),-1.0]])]});
            var Q20;
            Q20=makeQuery(id+"F3.imprint","IMPRINT",FACE,{"disambiguationData":[TD([[makeQuery(id+"F3.imprint","IMPRINT",EDGE,{"derivedFrom":sQuery(id+"F3.wireOp",EDGE,"E6.20.0.0")}),-1.0]])]});
            var Q21;
            Q21=makeQuery(id+"F3.imprint","IMPRINT",FACE,{"disambiguationData":[TD([[makeQuery(id+"F3.imprint","IMPRINT",EDGE,{"derivedFrom":sQuery(id+"F3.wireOp",EDGE,"E6.21.0.0")}),-1.0]])]});
            var Q22;
            Q22=makeQuery(id+"F3.imprint","IMPRINT",FACE,{"disambiguationData":[TD([[makeQuery(id+"F3.imprint","IMPRINT",EDGE,{"derivedFrom":sQuery(id+"F3.wireOp",EDGE,"E6.22.0.0")}),-1.0]])]});
            var Q23;
            Q23=makeQuery(id+"F3.imprint","IMPRINT",FACE,{"disambiguationData":[TD([[makeQuery(id+"F3.imprint","IMPRINT",EDGE,{"derivedFrom":sQuery(id+"F3.wireOp",EDGE,"E6.23.0.0")}),-1.0]])]});
            var Q24;
            Q24=makeQuery(id+"F3.imprint","IMPRINT",FACE,{"disambiguationData":[TD([[makeQuery(id+"F3.imprint","IMPRINT",EDGE,{"derivedFrom":sQuery(id+"F3.wireOp",EDGE,"E6.24.0.0")}),-1.0]])]});
            var Q25;
            Q25=makeQuery(id+"F3.imprint","IMPRINT",FACE,{"disambiguationData":[TD([[makeQuery(id+"F3.imprint","IMPRINT",EDGE,{"derivedFrom":sQuery(id+"F3.wireOp",EDGE,"E6.25.0.0")}),-1.0]])]});
            var Q26;
            Q26=makeQuery(id+"F3.imprint","IMPRINT",FACE,{"disambiguationData":[TD([[makeQuery(id+"F3.imprint","IMPRINT",EDGE,{"derivedFrom":sQuery(id+"F3.wireOp",EDGE,"E6.26.0.0")}),-1.0]])]});
            var Q27;
            Q27=makeQuery(id+"F3.imprint","IMPRINT",FACE,{"disambiguationData":[TD([[makeQuery(id+"F3.imprint","IMPRINT",EDGE,{"derivedFrom":sQuery(id+"F3.wireOp",EDGE,"E6.27.0.0")}),-1.0]])]});
            var Q28;
            Q28=makeQuery(id+"F3.imprint","IMPRINT",FACE,{"disambiguationData":[TD([[makeQuery(id+"F3.imprint","IMPRINT",EDGE,{"derivedFrom":sQuery(id+"F3.wireOp",EDGE,"E6.28.0.0")}),-1.0]])]});
            var Q29;
            Q29=makeQuery(id+"F3.imprint","IMPRINT",FACE,{"disambiguationData":[TD([[makeQuery(id+"F3.imprint","IMPRINT",EDGE,{"derivedFrom":sQuery(id+"F3.wireOp",EDGE,"E6.15.0.0")}),-1.0]])]});
            var Q30;
            Q30=makeQuery(id+"F3.imprint","IMPRINT",FACE,{"disambiguationData":[TD([[makeQuery(id+"F3.imprint","IMPRINT",EDGE,{"derivedFrom":sQuery(id+"F3.wireOp",EDGE,"E6.29.0.0")}),-1.0]])]});
            var Q31;
            Q31=makeQuery(id+"F3.imprint","IMPRINT",FACE,{"disambiguationData":[TD([[makeQuery(id+"F3.imprint","IMPRINT",EDGE,{"derivedFrom":sQuery(id+"F3.wireOp",EDGE,"E7.0.30.0")}),-1.0]])]});
            var Q32;
            Q32=makeQuery(id+"F3.imprint","IMPRINT",FACE,{"disambiguationData":[TD([[makeQuery(id+"F3.imprint","IMPRINT",EDGE,{"derivedFrom":sQuery(id+"F3.wireOp",EDGE,"E7.0.31.0")}),-1.0]])]});
            var Q33;
            Q33=makeQuery(id+"F3.imprint","IMPRINT",FACE,{"disambiguationData":[TD([[makeQuery(id+"F3.imprint","IMPRINT",EDGE,{"derivedFrom":sQuery(id+"F3.wireOp",EDGE,"E7.0.32.0")}),-1.0]])]});
            var Q34;
            Q34=makeQuery(id+"F3.imprint","IMPRINT",FACE,{"disambiguationData":[TD([[makeQuery(id+"F3.imprint","IMPRINT",EDGE,{"derivedFrom":sQuery(id+"F3.wireOp",EDGE,"E7.0.33.0")}),-1.0]])]});
            var Q35;
            Q35=makeQuery(id+"F3.imprint","IMPRINT",FACE,{"disambiguationData":[TD([[makeQuery(id+"F3.imprint","IMPRINT",EDGE,{"derivedFrom":sQuery(id+"F3.wireOp",EDGE,"E7.0.34.0")}),-1.0]])]});
            var Q36;
            Q36=makeQuery(id+"F3.imprint","IMPRINT",FACE,{"disambiguationData":[TD([[makeQuery(id+"F3.imprint","IMPRINT",EDGE,{"derivedFrom":sQuery(id+"F3.wireOp",EDGE,"E8.0.35.0")}),-1.0]])]});
            var Q37;
            Q37=makeQuery(id+"F3.imprint","IMPRINT",FACE,{"disambiguationData":[TD([[makeQuery(id+"F3.imprint","IMPRINT",EDGE,{"derivedFrom":sQuery(id+"F3.wireOp",EDGE,"E8.0.36.0")}),-1.0]])]});
            var Q38;
            Q38=makeQuery(id+"F3.imprint","IMPRINT",FACE,{"disambiguationData":[TD([[makeQuery(id+"F3.imprint","IMPRINT",EDGE,{"derivedFrom":sQuery(id+"F3.wireOp",EDGE,"E9")}),-1.0]])]});
            var Q39;
            Q39=makeQuery(id+"F3.imprint","IMPRINT",FACE,{"disambiguationData":[TD([[makeQuery(id+"F3.imprint","IMPRINT",EDGE,{"derivedFrom":sQuery(id+"F3.wireOp",EDGE,"E12.1.0.0")}),-1.0]])]});
            var Q40;
            Q40=makeQuery(id+"F3.imprint","IMPRINT",FACE,{"disambiguationData":[TD([[makeQuery(id+"F3.imprint","IMPRINT",EDGE,{"derivedFrom":sQuery(id+"F3.wireOp",EDGE,"E12.2.0.0")}),-1.0]])]});
            var Q41;
            Q41=makeQuery(id+"F3.imprint","IMPRINT",FACE,{"disambiguationData":[TD([[makeQuery(id+"F3.imprint","IMPRINT",EDGE,{"derivedFrom":sQuery(id+"F3.wireOp",EDGE,"E12.3.0.0")}),-1.0]])]});
            var Q42;
            Q42=makeQuery(id+"F3.imprint","IMPRINT",FACE,{"disambiguationData":[TD([[makeQuery(id+"F3.imprint","IMPRINT",EDGE,{"derivedFrom":sQuery(id+"F3.wireOp",EDGE,"E12.4.0.0")}),-1.0]])]});
            var Q43;
            Q43=makeQuery(id+"F3.imprint","IMPRINT",FACE,{"disambiguationData":[TD([[makeQuery(id+"F3.imprint","IMPRINT",EDGE,{"derivedFrom":sQuery(id+"F3.wireOp",EDGE,"E12.5.0.0")}),-1.0]])]});
            var Q44;
            Q44=makeQuery(id+"F3.imprint","IMPRINT",FACE,{"disambiguationData":[TD([[makeQuery(id+"F3.imprint","IMPRINT",EDGE,{"derivedFrom":sQuery(id+"F3.wireOp",EDGE,"E12.6.0.0")}),-1.0]])]});
            var Q45;
            Q45=makeQuery(id+"F3.imprint","IMPRINT",FACE,{"disambiguationData":[TD([[makeQuery(id+"F3.imprint","IMPRINT",EDGE,{"derivedFrom":sQuery(id+"F3.wireOp",EDGE,"E12.7.0.0")}),-1.0]])]});
            var Q46;
            Q46=makeQuery(id+"F3.imprint","IMPRINT",FACE,{"disambiguationData":[TD([[makeQuery(id+"F3.imprint","IMPRINT",EDGE,{"derivedFrom":sQuery(id+"F3.wireOp",EDGE,"E12.8.0.0")}),-1.0]])]});
            var Q47;
            Q47=makeQuery(id+"F3.imprint","IMPRINT",FACE,{"disambiguationData":[TD([[makeQuery(id+"F3.imprint","IMPRINT",EDGE,{"derivedFrom":sQuery(id+"F3.wireOp",EDGE,"E12.9.0.0")}),-1.0]])]});
            var Q48;
            Q48=makeQuery(id+"F3.imprint","IMPRINT",FACE,{"disambiguationData":[TD([[makeQuery(id+"F3.imprint","IMPRINT",EDGE,{"derivedFrom":sQuery(id+"F3.wireOp",EDGE,"E12.10.0.0")}),-1.0]])]});
            var Q49;
            Q49=makeQuery(id+"F3.imprint","IMPRINT",FACE,{"disambiguationData":[TD([[makeQuery(id+"F3.imprint","IMPRINT",EDGE,{"derivedFrom":sQuery(id+"F3.wireOp",EDGE,"E12.11.0.0")}),-1.0]])]});
            var Q50;
            Q50=makeQuery(id+"F3.imprint","IMPRINT",FACE,{"disambiguationData":[TD([[makeQuery(id+"F3.imprint","IMPRINT",EDGE,{"derivedFrom":sQuery(id+"F3.wireOp",EDGE,"E12.12.0.0")}),-1.0]])]});
            var Q51;
            Q51=makeQuery(id+"F3.imprint","IMPRINT",FACE,{"disambiguationData":[TD([[makeQuery(id+"F3.imprint","IMPRINT",EDGE,{"derivedFrom":sQuery(id+"F3.wireOp",EDGE,"E12.13.0.0")}),-1.0]])]});
            var Q52;
            Q52=makeQuery(id+"F3.imprint","IMPRINT",FACE,{"disambiguationData":[TD([[makeQuery(id+"F3.imprint","IMPRINT",EDGE,{"derivedFrom":sQuery(id+"F3.wireOp",EDGE,"E12.14.0.0")}),-1.0]])]});
            var Q53;
            Q53=makeQuery(id+"F3.imprint","IMPRINT",FACE,{"disambiguationData":[TD([[makeQuery(id+"F3.imprint","IMPRINT",EDGE,{"derivedFrom":sQuery(id+"F3.wireOp",EDGE,"E12.15.0.0")}),-1.0]])]});
            var Q54;
            Q54=makeQuery(id+"F3.imprint","IMPRINT",FACE,{"disambiguationData":[TD([[makeQuery(id+"F3.imprint","IMPRINT",EDGE,{"derivedFrom":sQuery(id+"F3.wireOp",EDGE,"E12.16.0.0")}),-1.0]])]});
            var Q55;
            Q55=makeQuery(id+"F3.imprint","IMPRINT",FACE,{"disambiguationData":[TD([[makeQuery(id+"F3.imprint","IMPRINT",EDGE,{"derivedFrom":sQuery(id+"F3.wireOp",EDGE,"E12.17.0.0")}),-1.0]])]});
            var Q56;
            Q56=makeQuery(id+"F3.imprint","IMPRINT",FACE,{"disambiguationData":[TD([[makeQuery(id+"F3.imprint","IMPRINT",EDGE,{"derivedFrom":sQuery(id+"F3.wireOp",EDGE,"E12.18.0.0")}),-1.0]])]});
            var Q57;
            Q57=makeQuery(id+"F3.imprint","IMPRINT",FACE,{"disambiguationData":[TD([[makeQuery(id+"F3.imprint","IMPRINT",EDGE,{"derivedFrom":sQuery(id+"F3.wireOp",EDGE,"E12.19.0.0")}),-1.0]])]});
            var Q58;
            Q58=makeQuery(id+"F3.imprint","IMPRINT",FACE,{"disambiguationData":[TD([[makeQuery(id+"F3.imprint","IMPRINT",EDGE,{"derivedFrom":sQuery(id+"F3.wireOp",EDGE,"E12.20.0.0")}),-1.0]])]});
            var Q59;
            Q59=makeQuery(id+"F3.imprint","IMPRINT",FACE,{"disambiguationData":[TD([[makeQuery(id+"F3.imprint","IMPRINT",EDGE,{"derivedFrom":sQuery(id+"F3.wireOp",EDGE,"E12.21.0.0")}),-1.0]])]});
            var Q60;
            Q60=makeQuery(id+"F3.imprint","IMPRINT",FACE,{"disambiguationData":[TD([[makeQuery(id+"F3.imprint","IMPRINT",EDGE,{"derivedFrom":sQuery(id+"F3.wireOp",EDGE,"E12.22.0.0")}),-1.0]])]});
            var Q61;
            Q61=makeQuery(id+"F3.imprint","IMPRINT",FACE,{"disambiguationData":[TD([[makeQuery(id+"F3.imprint","IMPRINT",EDGE,{"derivedFrom":sQuery(id+"F3.wireOp",EDGE,"E12.23.0.0")}),-1.0]])]});
            var Q62;
            Q62=makeQuery(id+"F3.imprint","IMPRINT",FACE,{"disambiguationData":[TD([[makeQuery(id+"F3.imprint","IMPRINT",EDGE,{"derivedFrom":sQuery(id+"F3.wireOp",EDGE,"E12.24.0.0")}),-1.0]])]});
            var Q63;
            Q63=makeQuery(id+"F3.imprint","IMPRINT",FACE,{"disambiguationData":[TD([[makeQuery(id+"F3.imprint","IMPRINT",EDGE,{"derivedFrom":sQuery(id+"F3.wireOp",EDGE,"E12.26.0.0")}),-1.0]])]});
            var Q64;
            Q64=makeQuery(id+"F3.imprint","IMPRINT",FACE,{"disambiguationData":[TD([[makeQuery(id+"F3.imprint","IMPRINT",EDGE,{"derivedFrom":sQuery(id+"F3.wireOp",EDGE,"E12.27.0.0")}),-1.0]])]});
            var Q65;
            Q65=makeQuery(id+"F3.imprint","IMPRINT",FACE,{"disambiguationData":[TD([[makeQuery(id+"F3.imprint","IMPRINT",EDGE,{"derivedFrom":sQuery(id+"F3.wireOp",EDGE,"E12.28.0.0")}),-1.0]])]});
            var Q66;
            Q66=makeQuery(id+"F3.imprint","IMPRINT",FACE,{"disambiguationData":[TD([[makeQuery(id+"F3.imprint","IMPRINT",EDGE,{"derivedFrom":sQuery(id+"F3.wireOp",EDGE,"E12.29.0.0")}),-1.0]])]});
            var Q67;
            Q67=makeQuery(id+"F3.imprint","IMPRINT",FACE,{"disambiguationData":[TD([[makeQuery(id+"F3.imprint","IMPRINT",EDGE,{"derivedFrom":sQuery(id+"F3.wireOp",EDGE,"E12.32.0.0")}),-1.0]])]});
            var Q68;
            Q68=makeQuery(id+"F3.imprint","IMPRINT",FACE,{"disambiguationData":[TD([[makeQuery(id+"F3.imprint","IMPRINT",EDGE,{"derivedFrom":sQuery(id+"F3.wireOp",EDGE,"E12.33.0.0")}),-1.0]])]});
            var Q69;
            Q69=makeQuery(id+"F3.imprint","IMPRINT",FACE,{"disambiguationData":[TD([[makeQuery(id+"F3.imprint","IMPRINT",EDGE,{"derivedFrom":sQuery(id+"F3.wireOp",EDGE,"E12.34.0.0")}),-1.0]])]});
            var Q70;
            Q70=makeQuery(id+"F3.imprint","IMPRINT",FACE,{"disambiguationData":[TD([[makeQuery(id+"F3.imprint","IMPRINT",EDGE,{"derivedFrom":sQuery(id+"F3.wireOp",EDGE,"E12.35.0.0")}),-1.0]])]});
            var Q71;
            Q71=makeQuery(id+"F3.imprint","IMPRINT",FACE,{"disambiguationData":[TD([[makeQuery(id+"F3.imprint","IMPRINT",EDGE,{"derivedFrom":sQuery(id+"F3.wireOp",EDGE,"E12.36.0.0")}),-1.0]])]});
            var Q72;
            Q72=makeQuery(id+"F3.imprint","IMPRINT",FACE,{"disambiguationData":[TD([[makeQuery(id+"F3.imprint","IMPRINT",EDGE,{"derivedFrom":sQuery(id+"F3.wireOp",EDGE,"E12.25.0.0")}),-1.0]])]});
            var Q73;
            Q73=makeQuery(id+"F3.imprint","IMPRINT",FACE,{"disambiguationData":[TD([[makeQuery(id+"F3.imprint","IMPRINT",EDGE,{"derivedFrom":sQuery(id+"F3.wireOp",EDGE,"E12.30.0.0")}),-1.0]])]});
            var Q74;
            Q74=makeQuery(id+"F3.imprint","IMPRINT",FACE,{"disambiguationData":[TD([[makeQuery(id+"F3.imprint","IMPRINT",EDGE,{"derivedFrom":sQuery(id+"F3.wireOp",EDGE,"E12.31.0.0")}),-1.0]])]});
            extrude(context, id + "F4", {"entities" : qUnion([Q0, Q1, Q2, Q3, Q4, Q5, Q6, Q7, Q8, Q9, Q10, Q11, Q12, Q13, Q14, Q15, Q16, Q17, Q18, Q19, Q20, Q21, Q22, Q23, Q24, Q25, Q26, Q27, Q28, Q29, Q30, Q31, Q32, Q33, Q34, Q35, Q36, Q37, Q38, Q39, Q40, Q41, Q42, Q43, Q44, Q45, Q46, Q47, Q48, Q49, Q50, Q51, Q52, Q53, Q54, Q55, Q56, Q57, Q58, Q59, Q60, Q61, Q62, Q63, Q64, Q65, Q66, Q67, Q68, Q69, Q70, Q71, Q72, Q73, Q74]), "operationType" : NewBodyOperationType.ADD, "endBound" : BoundingType.SYMMETRIC, "depth" : 25 * mm});
        }
    });
